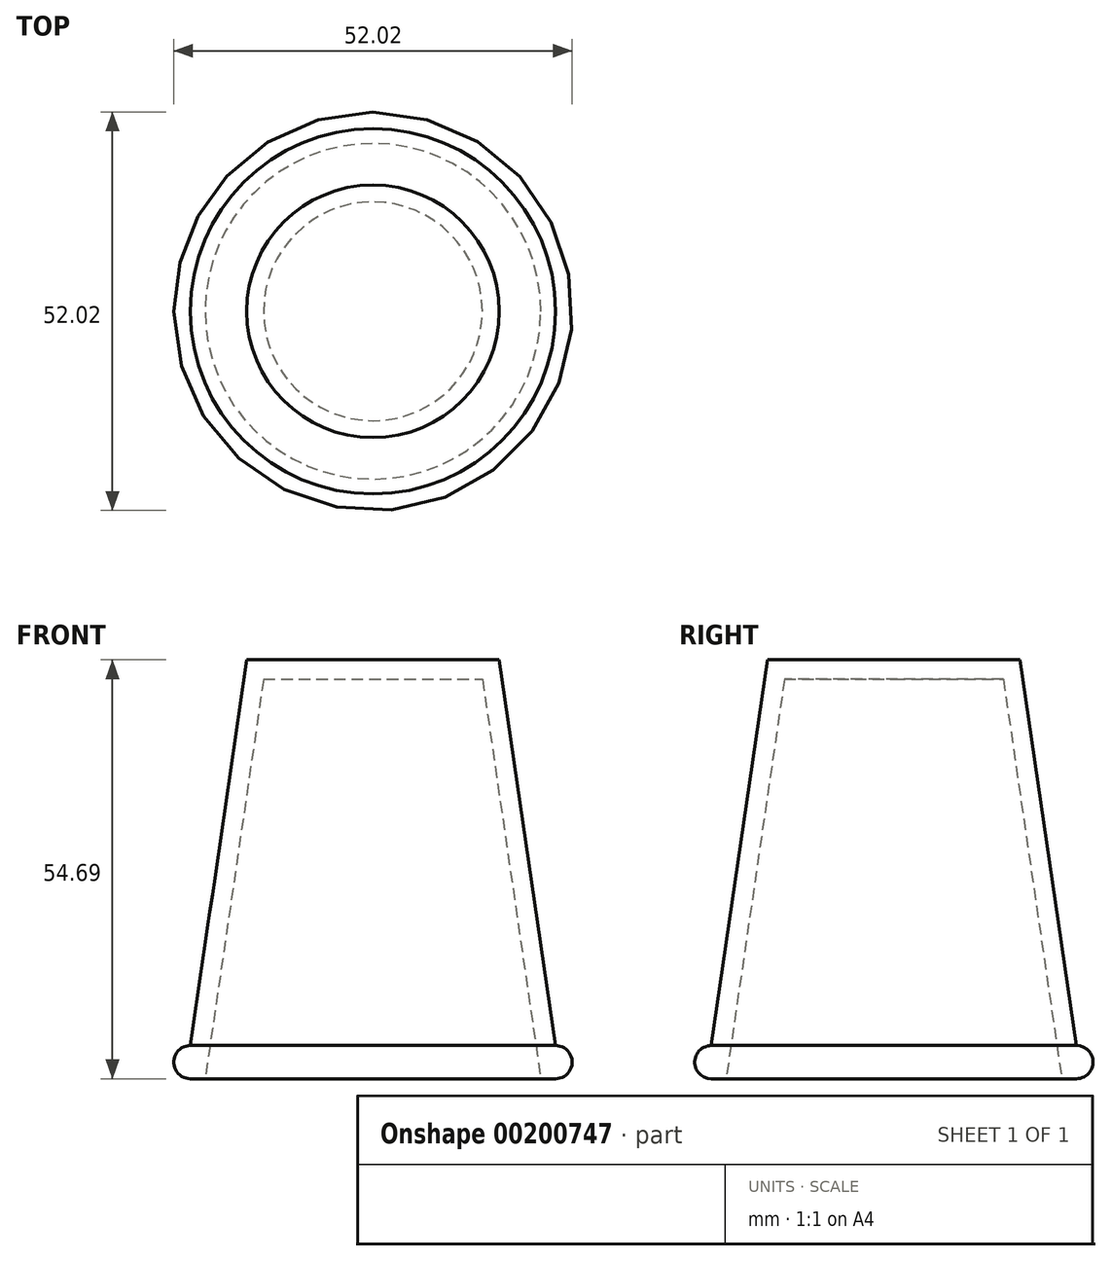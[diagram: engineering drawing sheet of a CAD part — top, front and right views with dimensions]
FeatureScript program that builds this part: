
annotation { "Feature Type Name" : "Feature", "Feature Type Description" : "" }
export const myFeature = defineFeature(function(context is Context, id is Id, definition is map)
    precondition{}
    {
        {
            var Q0;
            Q0=qCreatedBy(makeId("Front.planeOp"),FACE);
            var sketch = newSketch(context, id + "F0", { "sketchPlane" : qUnion([Q0])});
            skLineSegment(sketch, "E0", {"start": v(0, 0) * mm, "end": v(0, 50.36) * mm});
            skLineSegment(sketch, "E1", {"start": v(0, 50.36) * mm, "end": v(16.48, 50.36) * mm});
            skLineSegment(sketch, "E2", {"start": v(0, 0) * mm, "end": v(23.85, 0) * mm});
            skLineSegment(sketch, "E3", {"start": v(23.85, 0) * mm, "end": v(16.48, 50.36) * mm});
            skLineSegment(sketch, "E4", {"start": v(0, 0) * mm, "end": v(0, -4.33) * mm});
            skLineSegment(sketch, "E5", {"start": v(0, -4.33) * mm, "end": v(23.85, -4.33) * mm});
            skArc(sketch, "E6", {"start": v(23.85, -4.33) * mm, "mid": v(26.01, -2.16) * mm, "end": v(23.85, 0) * mm});
            skSolve(sketch);
        }
        {
            var Q0;
            Q0 = qSketchRegion(id + "F0", true);
            var Q1;
            Q1=sQuery(id+"F0.wireOp",EDGE,"E0");
            revolve(context, id + "F1", {"entities" : qUnion([Q0]), "axis" : qUnion([Q1]), "revolveType" : RevolveType.FULL});
        }
        {
            var Q0;
            Q0=makeQuery(id+"F1.opRevolve","SWEPT_FACE",FACE,{"disambiguationData":[OSD([sQuery(id+"F0.wireOp",EDGE,"E5")])]});
            shell(context, id + "F2", {"entities" : qUnion([Q0]), "thickness" : 2.54 * mm});
        }
    });
